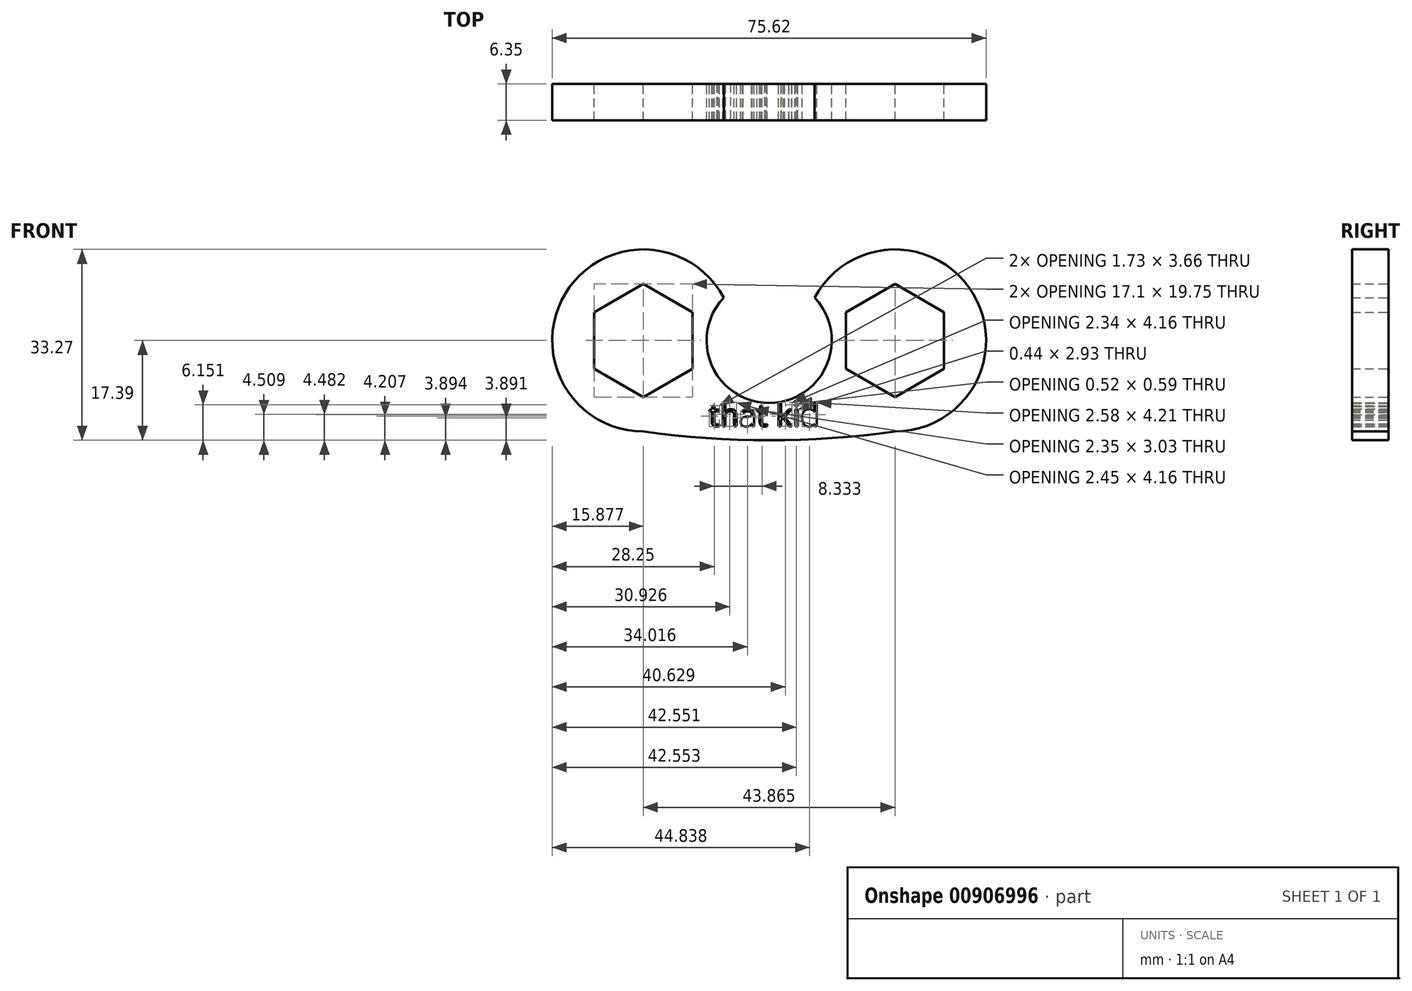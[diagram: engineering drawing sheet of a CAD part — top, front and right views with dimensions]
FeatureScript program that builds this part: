
annotation { "Feature Type Name" : "Feature", "Feature Type Description" : "" }
export const myFeature = defineFeature(function(context is Context, id is Id, definition is map)
    precondition{}
    {
        {
            var Q0;
            Q0=qCreatedBy(makeId("Front.planeOp"),FACE);
            var sketch = newSketch(context, id + "F0", { "sketchPlane" : qUnion([Q0])});
            skCircle(sketch, "E0", {"center": v(0, 0) * mm, "radius": 10.9 * mm});
            skArc(sketch, "E1", {"start": v(-7.93, 7.48) * mm, "mid": v(-37.8, 0) * mm, "end": v(-7.93, -7.48) * mm});
            skCircle(sketch, "E2.cCircle", {"center": v(-21.93, 0) * mm, "radius": 8.55 * mm, "construction": true});
            skLineSegment(sketch, "E2.0", {"start": v(-13.38, 4.94) * mm, "end": v(-13.38, -4.94) * mm});
            skLineSegment(sketch, "E2.1", {"start": v(-13.38, -4.94) * mm, "end": v(-21.93, -9.87) * mm});
            skLineSegment(sketch, "E2.2", {"start": v(-21.93, -9.87) * mm, "end": v(-30.48, -4.94) * mm});
            skLineSegment(sketch, "E2.3", {"start": v(-30.48, -4.94) * mm, "end": v(-30.48, 4.94) * mm});
            skLineSegment(sketch, "E2.4", {"start": v(-30.48, 4.94) * mm, "end": v(-21.93, 9.87) * mm});
            skLineSegment(sketch, "E2.5", {"start": v(-21.93, 9.87) * mm, "end": v(-13.38, 4.94) * mm});
            skPoint(sketch, "E2.0.midPoint", {"position": v(-13.38, 0) * mm});
            skArc(sketch, "E3.MirrorCS", {"start": v(7.93, 7.48) * mm, "mid": v(37.8, 0) * mm, "end": v(7.93, -7.48) * mm});
            skLineSegment(sketch, "E4.MirrorCS", {"start": v(13.38, 4.94) * mm, "end": v(13.38, -4.94) * mm});
            skLineSegment(sketch, "E5.MirrorCS", {"start": v(30.48, 4.94) * mm, "end": v(21.93, 9.87) * mm});
            skLineSegment(sketch, "E6.MirrorCS", {"start": v(13.38, -4.94) * mm, "end": v(21.93, -9.87) * mm});
            skLineSegment(sketch, "E7.MirrorCS", {"start": v(21.93, 9.87) * mm, "end": v(13.38, 4.94) * mm});
            skLineSegment(sketch, "E8.MirrorCS", {"start": v(30.48, -4.94) * mm, "end": v(30.48, 4.94) * mm});
            skLineSegment(sketch, "E9.MirrorCS", {"start": v(21.93, -9.87) * mm, "end": v(30.48, -4.94) * mm});
            skCircle(sketch, "E10.MirrorC", {"center": v(21.93, 0) * mm, "radius": 8.55 * mm, "construction": true});
            skPoint(sketch, "E11.MirrorP", {"position": v(13.38, 0) * mm});
            skArc(sketch, "E12", {"start": v(-21.93, -15.88) * mm, "mid": v(0, -17.39) * mm, "end": v(21.93, -15.88) * mm});
            skArc(sketch, "E13.MirrorCS", {"start": v(-21.93, 15.88) * mm, "mid": v(0, 17.39) * mm, "end": v(21.93, 15.88) * mm});
            skText(sketch, "E14", { "text": "that kid\n", "fontName": "OpenSans-Regular.ttf"});
            const initialGuessF0  = {"E14": [-0.01051, -0.01496, 1, 0, 0.00394]};
            skSetInitialGuess(sketch, initialGuessF0);
            skSolve(sketch);
        }
        {
            var Q0;
            {var subQ5=sQuery(id+"F0.wireOp",EDGE,"E12");Q0=makeQuery(id+"F0.imprint","IMPRINT",FACE,{"disambiguationData":[TD([[makeQuery(id+"F0.imprint","IMPRINT",EDGE,{"derivedFrom":subQ5}),1.0]])]});}
            var Q1;
            {var subQ5=sQuery(id+"F0.wireOp",EDGE,"E13.MirrorCS");Q1=makeQuery(id+"F0.imprint","IMPRINT",FACE,{"disambiguationData":[TD([[makeQuery(id+"F0.imprint","IMPRINT",EDGE,{"derivedFrom":subQ5}),-1.0]])]});}
            var Q2;
            Q2=makeQuery(id+"F0.imprint","IMPRINT",FACE,{"disambiguationData":[TD([[makeQuery(id+"F0.imprint","IMPRINT",EDGE,{"derivedFrom":sQuery(id+"F0.wireOp",EDGE,"E2.0")}),1.0]])]});
            var Q3;
            Q3=makeQuery(id+"F0.imprint","IMPRINT",FACE,{"disambiguationData":[TD([[makeQuery(id+"F0.imprint","IMPRINT",EDGE,{"derivedFrom":sQuery(id+"F0.wireOp",EDGE,"E4.MirrorCS")}),-1.0]])]});
            extrude(context, id + "F1", {"entities" : qUnion([Q0, Q1, Q2, Q3]), "depth" : 6.35 * mm, "offsetDistance" : 25.4 * mm});
        }
    });
